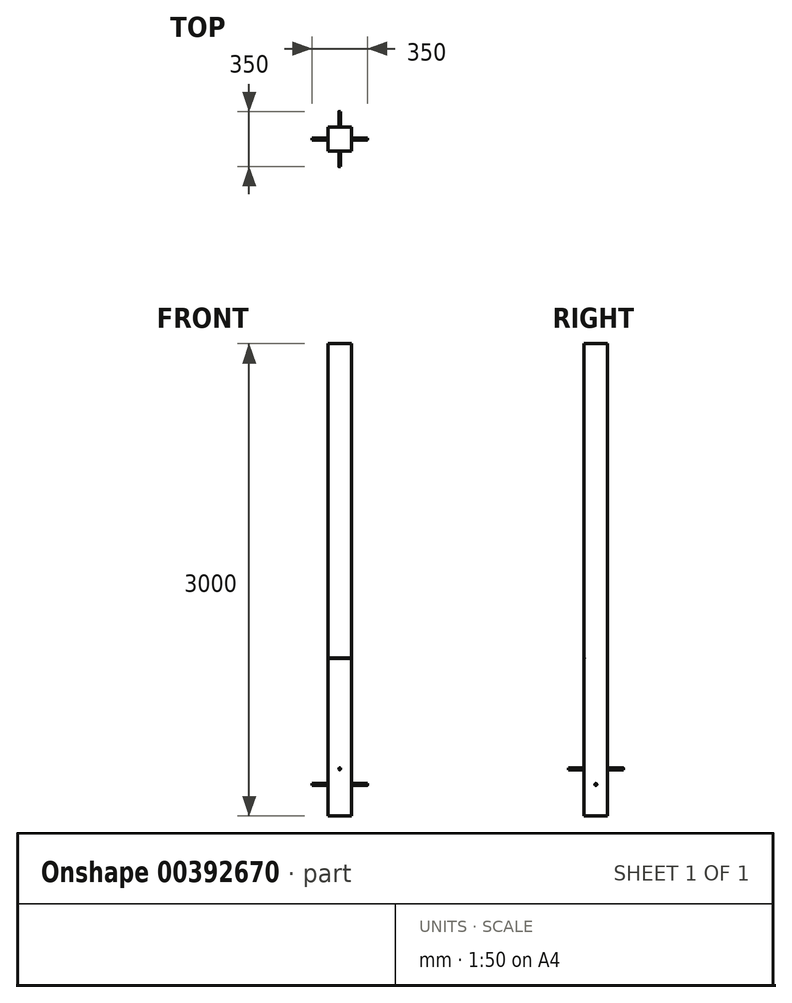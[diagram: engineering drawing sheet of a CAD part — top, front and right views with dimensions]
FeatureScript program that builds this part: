
annotation { "Feature Type Name" : "Feature", "Feature Type Description" : "" }
export const myFeature = defineFeature(function(context is Context, id is Id, definition is map)
    precondition{}
    {
        {
            var Q0;
            Q0=qCreatedBy(makeId("Top.planeOp"),FACE);
            var sketch = newSketch(context, id + "F0", { "sketchPlane" : qUnion([Q0])});
            skLineSegment(sketch, "E0.bottom", {"start": v(-75, -75) * mm, "end": v(75, -75) * mm});
            skLineSegment(sketch, "E0.top", {"start": v(-75, 75) * mm, "end": v(75, 75) * mm});
            skLineSegment(sketch, "E0.left", {"start": v(-75, -75) * mm, "end": v(-75, 75) * mm});
            skLineSegment(sketch, "E0.right", {"start": v(75, -75) * mm, "end": v(75, 75) * mm});
            skPoint(sketch, "E0.middle", {"position": v(0, 0) * mm});
            skSolve(sketch);
        }
        {
            var Q0;
            Q0 = qSketchRegion(id + "F0", true);
            extrude(context, id + "F1", {"entities" : qUnion([Q0]), "depth" : 3000 * mm});
        }
        {
            var Q0;
            Q0=makeQuery(id+"F1.opExtrude","SWEPT_FACE",FACE,{"disambiguationData":[OSD([sQuery(id+"F0.wireOp",EDGE,"E0.bottom")])]});
            var sketch = newSketch(context, id + "F2", { "sketchPlane" : qUnion([Q0])});
            skLineSegment(sketch, "E1", {"start": v(0, 0) * mm, "end": v(0, 300) * mm});
            skPoint(sketch, "E1.endSnap0", {"position": v(0, 0) * mm});
            skCircle(sketch, "E2", {"center": v(0, 300) * mm, "radius": 6 * mm});
            skSolve(sketch);
        }
        {
            var Q0;
            Q0 = qSketchRegion(id + "F2", true);
            extrude(context, id + "F3", {"entities" : qUnion([Q0]), "operationType" : NewBodyOperationType.ADD, "depth" : 100 * mm});
        }
        {
            var Q0;
            Q0=makeQuery(id+"F1.opExtrude","SWEPT_FACE",FACE,{"disambiguationData":[OSD([sQuery(id+"F0.wireOp",EDGE,"E0.top")])]});
            var sketch = newSketch(context, id + "F4", { "sketchPlane" : qUnion([Q0])});
            skLineSegment(sketch, "E3", {"start": v(0, 0) * mm, "end": v(0, 300) * mm});
            skCircle(sketch, "E4", {"center": v(0, 300) * mm, "radius": 6 * mm});
            skSolve(sketch);
        }
        {
            var Q0;
            Q0 = qSketchRegion(id + "F4", true);
            extrude(context, id + "F5", {"entities" : qUnion([Q0]), "operationType" : NewBodyOperationType.ADD, "depth" : 100 * mm});
        }
        {
            var Q0;
            Q0=makeQuery(id+"F1.opExtrude","SWEPT_FACE",FACE,{"disambiguationData":[OSD([sQuery(id+"F0.wireOp",EDGE,"E0.right")])]});
            var sketch = newSketch(context, id + "F6", { "sketchPlane" : qUnion([Q0])});
            skLineSegment(sketch, "E5", {"start": v(0, 0) * mm, "end": v(0, 200) * mm});
            skCircle(sketch, "E6", {"center": v(0, 200) * mm, "radius": 6 * mm});
            skSolve(sketch);
        }
        {
            var Q0;
            Q0 = qSketchRegion(id + "F6", true);
            extrude(context, id + "F7", {"entities" : qUnion([Q0]), "operationType" : NewBodyOperationType.ADD, "depth" : 100 * mm});
        }
        {
            var Q0;
            Q0=makeQuery(id+"F1.opExtrude","SWEPT_FACE",FACE,{"disambiguationData":[OSD([sQuery(id+"F0.wireOp",EDGE,"E0.left")])]});
            var sketch = newSketch(context, id + "F8", { "sketchPlane" : qUnion([Q0])});
            skLineSegment(sketch, "E7", {"start": v(0, 0) * mm, "end": v(0, 200) * mm});
            skCircle(sketch, "E8", {"center": v(0, 200) * mm, "radius": 6 * mm});
            skSolve(sketch);
        }
        {
            var Q0;
            Q0 = qSketchRegion(id + "F8", true);
            extrude(context, id + "F9", {"entities" : qUnion([Q0]), "operationType" : NewBodyOperationType.ADD, "depth" : 100 * mm});
        }
        {
            var Q0;
            Q0=makeQuery(id+"F1.opExtrude","SWEPT_FACE",FACE,{"disambiguationData":[OSD([sQuery(id+"F0.wireOp",EDGE,"E0.bottom")])]});
            var sketch = newSketch(context, id + "F10", { "sketchPlane" : qUnion([Q0])});
            skLineSegment(sketch, "E9", {"start": v(75, 1000) * mm, "end": v(-75, 1000) * mm});
            skLineSegment(sketch, "E10", {"start": v(-75, 1000) * mm, "end": v(-75, 1005) * mm});
            skLineSegment(sketch, "E11", {"start": v(-75, 1005) * mm, "end": v(75, 1005) * mm});
            skLineSegment(sketch, "E12", {"start": v(75, 1005) * mm, "end": v(75, 1000) * mm});
            skSolve(sketch);
        }
        {
            var Q0;
            Q0 = qSketchRegion(id + "F10", true);
            extrude(context, id + "F11", {"entities" : qUnion([Q0]), "operationType" : NewBodyOperationType.REMOVE, "oppositeDirection" : true, "depth" : 3 * mm});
        }
    });
